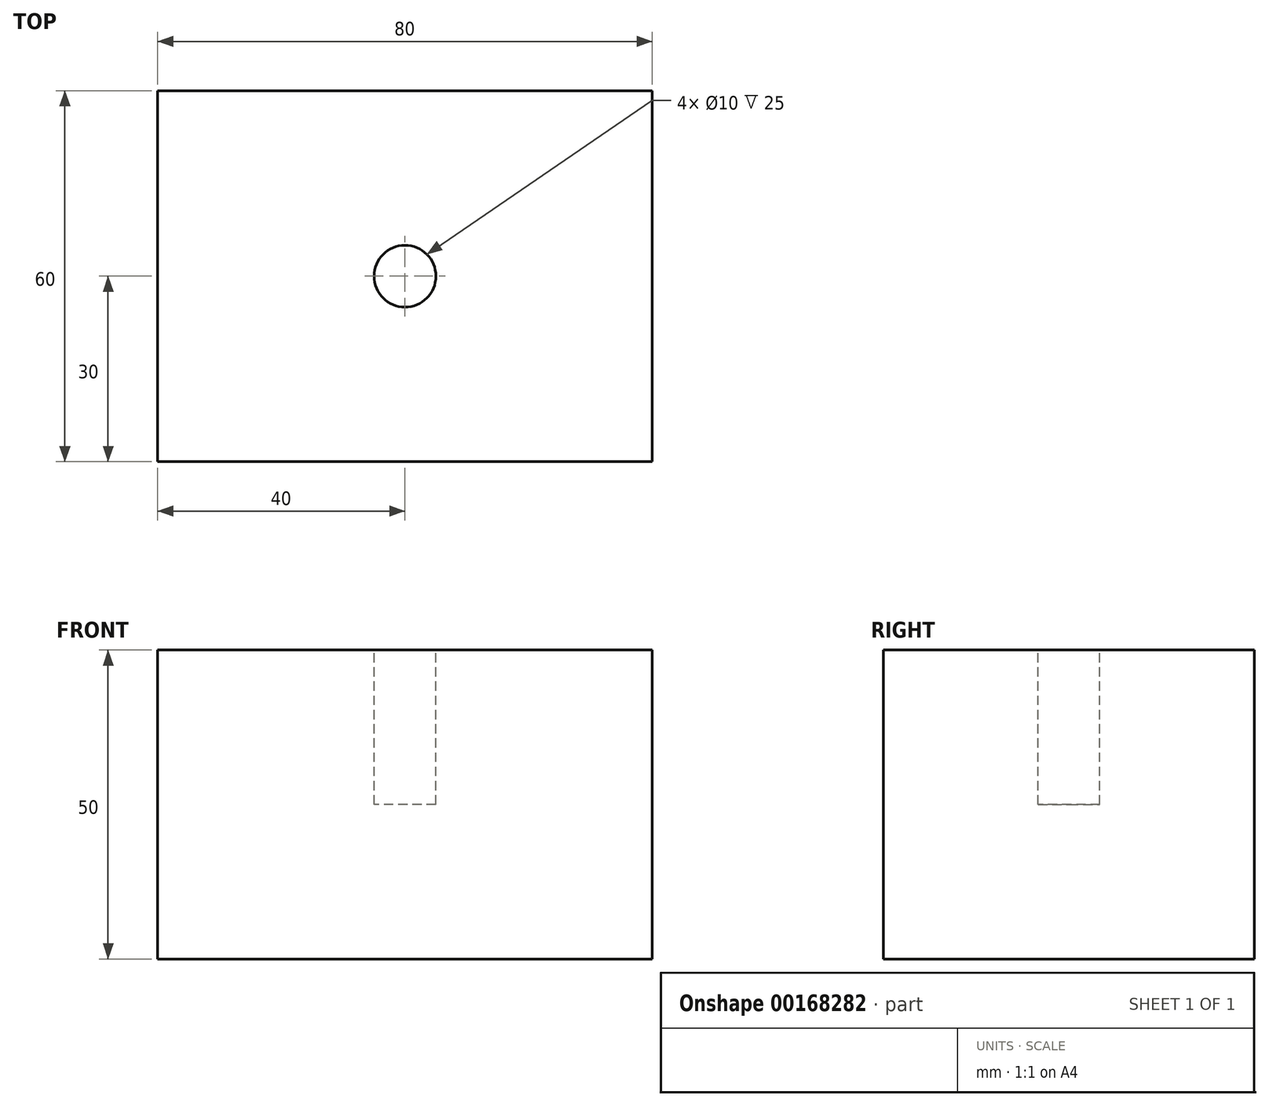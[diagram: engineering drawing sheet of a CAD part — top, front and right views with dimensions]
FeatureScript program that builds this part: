
annotation { "Feature Type Name" : "Feature", "Feature Type Description" : "" }
export const myFeature = defineFeature(function(context is Context, id is Id, definition is map)
    precondition{}
    {
        {
            var Q0;
            Q0=qCreatedBy(makeId("Top.planeOp"),FACE);
            var sketch = newSketch(context, id + "F0", { "sketchPlane" : qUnion([Q0])});
            skLineSegment(sketch, "E0.bottom", {"start": v(40, 30) * mm, "end": v(-40, 30) * mm});
            skLineSegment(sketch, "E0.top", {"start": v(40, -30) * mm, "end": v(-40, -30) * mm});
            skLineSegment(sketch, "E0.left", {"start": v(40, 30) * mm, "end": v(40, -30) * mm});
            skLineSegment(sketch, "E0.right", {"start": v(-40, 30) * mm, "end": v(-40, -30) * mm});
            skPoint(sketch, "E0.middle", {"position": v(0, 0) * mm});
            skSolve(sketch);
        }
        {
            var Q0;
            Q0 = qSketchRegion(id + "F0", true);
            extrude(context, id + "F1", {"entities" : qUnion([Q0]), "depth" : 50 * mm});
        }
        {
            var Q0;
            Q0=makeQuery(id+"F1.opExtrude","CAP_FACE",FACE,{"disambiguationData":[OSD([sQuery(id+"F0.wireOp",EDGE,"E0.bottom"),sQuery(id+"F0.wireOp",EDGE,"E0.top"),sQuery(id+"F0.wireOp",EDGE,"E0.left"),sQuery(id+"F0.wireOp",EDGE,"E0.right")])],"isStart":false});
            var sketch = newSketch(context, id + "F2", { "sketchPlane" : qUnion([Q0])});
            skCircle(sketch, "E1", {"center": v(0, 0) * mm, "radius": 5 * mm});
            skSolve(sketch);
        }
        {
            var Q0;
            Q0=makeQuery(id+"F2.imprint","IMPRINT",FACE,{"disambiguationData":[TD([[makeQuery(id+"F2.imprint","IMPRINT",EDGE,{"derivedFrom":sQuery(id+"F2.wireOp",EDGE,"E1")}),1.0]])]});
            var Q1;
            Q1=sQuery(id+"F2.wireOp",EDGE,"E1");
            extrude(context, id + "F3", {"entities" : qUnion([Q0]), "operationType" : NewBodyOperationType.REMOVE, "surfaceEntities" : qUnion([Q1]), "oppositeDirection" : true, "depth" : 25 * mm});
        }
    });
